# Revit family: Урна для раздельного сбора мусора «Алвариум» Арт 12846
name_source: partatom
category: Антураж
revit_build: Autodesk Revit 2018 (Build: 20180423_1000(x64)
units: mm (PartAtom-declared; Revit-internal decimal feet)

## family parameters
Всегда вертикально = Да
Источник визуального образа = Геометрия семейства
На основе рабочей плоскости = Нет
Общий = Нет
При загрузке вырезать с полостями = Нет
Точка расчета площади = Нет

## types (2) — shared parameters
URL = https://hobbyka.ru
Артикул товара = Арт. 12846
Высота = 650 мм
Группа модели = Уличные урны
Изготовитель = ООО «Хоббика»
Изображение типоразмера = Урна для раздельного сбора мусора «Алвариум» Арт 12846.jpg
Материал изделия = Сталь, дерево
Цвет отходов бак №1 = Желтый
Цвет отходов бак №2 = Синий
Цвет отходов бак №3 = Красный
Цвет урны = Сталь
Ширина = 390 мм

## per-type parameters (varying)
| type | 2 секции | 3 секции | Длина | Описание |
| Версия на 3 секции | Нет | Да | 1120 мм | Урна для раздельного сбора мусора «Алвариум». Версия на 3 секции |
| Версия на 2 секции | Да | Нет | 745 мм | Урна для раздельного сбора мусора «Алвариум». Версия на 2 секции |
